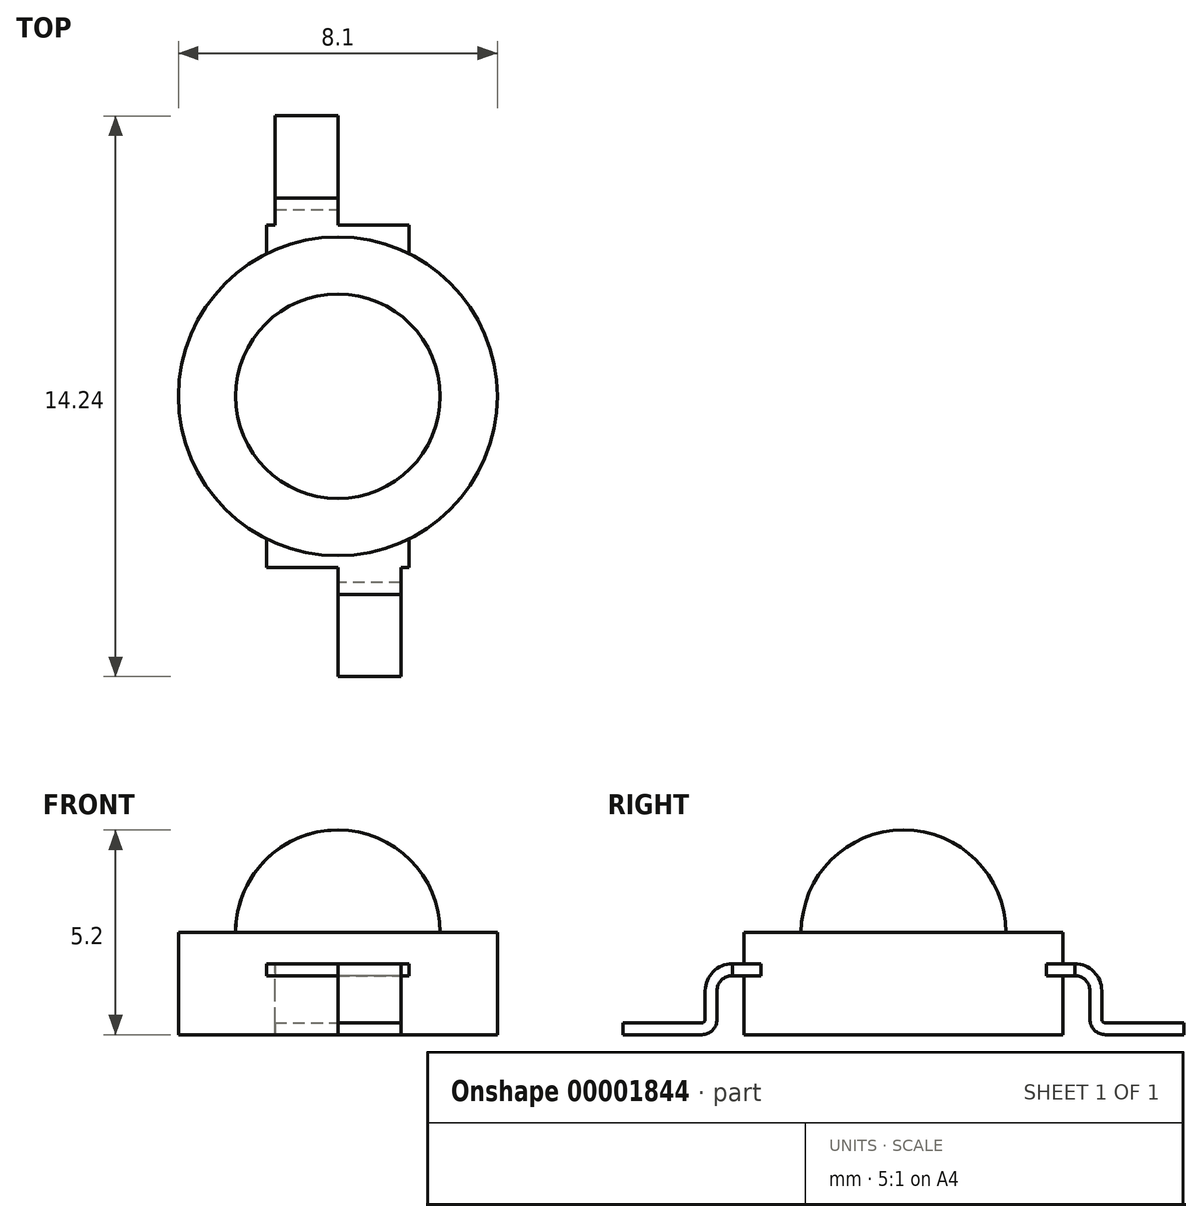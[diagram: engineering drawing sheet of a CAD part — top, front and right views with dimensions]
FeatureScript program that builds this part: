
annotation { "Feature Type Name" : "Feature", "Feature Type Description" : "" }
export const myFeature = defineFeature(function(context is Context, id is Id, definition is map)
    precondition{}
    {
        {
            var Q0;
            Q0=qCreatedBy(makeId("Front.planeOp"),FACE);
            var sketch = newSketch(context, id + "F0", { "sketchPlane" : qUnion([Q0])});
            skLineSegment(sketch, "E0", {"start": v(0, 0) * mm, "end": v(0, 5.2) * mm});
            skArc(sketch, "E1", {"start": v(0, 5.2) * mm, "mid": v(-1.84, 4.44) * mm, "end": v(-2.6, 2.6) * mm});
            skLineSegment(sketch, "E2", {"start": v(-2.6, 2.6) * mm, "end": v(-4.05, 2.6) * mm});
            skLineSegment(sketch, "E3", {"start": v(-4.05, 2.6) * mm, "end": v(-4.05, 0) * mm});
            skLineSegment(sketch, "E4", {"start": v(-4.05, 0) * mm, "end": v(0, 0) * mm});
            skSolve(sketch);
        }
        {
            var Q0;
            Q0=makeQuery(id+"F0.imprint","IMPRINT",FACE,{"disambiguationData":[TD([[makeQuery(id+"F0.imprint","IMPRINT",EDGE,{"derivedFrom":sQuery(id+"F0.wireOp",EDGE,"E0")}),1.0]])]});
            var Q1;
            Q1=sQuery(id+"F0.wireOp",EDGE,"E0");
            revolve(context, id + "F1", {"entities" : qUnion([Q0]), "axis" : qUnion([Q1]), "revolveType" : RevolveType.FULL});
        }
        {
            var Q0;
            Q0=qCreatedBy(makeId("Top.planeOp"),FACE);
            var sketch = newSketch(context, id + "F2", { "sketchPlane" : qUnion([Q0])});
            skLineSegment(sketch, "E5.bottom", {"start": v(-1.6, 7.12) * mm, "end": v(0, 7.12) * mm});
            skLineSegment(sketch, "E5.top", {"start": v(-1.6, 5.12) * mm, "end": v(0, 5.12) * mm});
            skLineSegment(sketch, "E5.left", {"start": v(-1.6, 7.12) * mm, "end": v(-1.6, 5.12) * mm});
            skLineSegment(sketch, "E5.right", {"start": v(0, 7.12) * mm, "end": v(0, 5.12) * mm});
            skLineSegment(sketch, "E6.bottom", {"start": v(-1.8, 4.05) * mm, "end": v(1.8, 4.05) * mm});
            skLineSegment(sketch, "E6.top", {"start": v(-1.8, 3.62) * mm, "end": v(1.8, 3.63) * mm});
            skLineSegment(sketch, "E6.left", {"start": v(-1.8, 4.05) * mm, "end": v(-1.8, 3.62) * mm});
            skLineSegment(sketch, "E6.right", {"start": v(1.8, 4.05) * mm, "end": v(1.8, 3.62) * mm});
            skLineSegment(sketch, "E7", {"start": v(0, 3.63) * mm, "end": v(0, 0) * mm, "construction": true});
            skLineSegment(sketch, "E8", {"start": v(0, 0) * mm, "end": v(-6.04, 0) * mm, "construction": true});
            skSolve(sketch);
        }
        {
            var Q0;
            Q0=makeQuery(id+"F2.imprint","IMPRINT",FACE,{"disambiguationData":[TD([[makeQuery(id+"F2.imprint","IMPRINT",EDGE,{"derivedFrom":sQuery(id+"F2.wireOp",EDGE,"E6.bottom")}),-1.0]])]});
            extrude(context, id + "F3", {"entities" : qUnion([Q0]), "operationType" : NewBodyOperationType.REMOVE, "endBound" : BoundingType.UP_TO_NEXT, "depth" : 25 * mm});
        }
        {
            var Q0;
            Q0=qCreatedBy(makeId("Top.planeOp"),FACE);
            cPlane(context, id + "F4", {"entities" : qUnion([Q0]), "cplaneType" : CPlaneType.OFFSET, "offset" : 1.5 * mm, "width" : 150 * mm, "height" : 150 * mm});
        }
        {
            var Q0;
            Q0=qCreatedBy(id+"F4.planeOp",FACE);
            var sketch = newSketch(context, id + "F5", { "sketchPlane" : qUnion([Q0])});
            skLineSegment(sketch, "E9.bottom", {"start": v(-1.8, 4.35) * mm, "end": v(1.8, 4.35) * mm});
            skLineSegment(sketch, "E9.top", {"start": v(-1.8, 3.63) * mm, "end": v(1.8, 3.63) * mm});
            skLineSegment(sketch, "E9.left", {"start": v(-1.8, 4.35) * mm, "end": v(-1.8, 3.62) * mm});
            skLineSegment(sketch, "E9.right", {"start": v(1.8, 4.35) * mm, "end": v(1.8, 3.62) * mm});
            skLineSegment(sketch, "E10", {"start": v(0, 3.63) * mm, "end": v(0, 0) * mm, "construction": true});
            skLineSegment(sketch, "E11", {"start": v(0, 0) * mm, "end": v(-5.3, 0) * mm, "construction": true});
            skSolve(sketch);
        }
        {
            var Q0;
            Q0 = qSketchRegion(id + "F5", true);
            extrude(context, id + "F6", {"entities" : qUnion([Q0]), "operationType" : NewBodyOperationType.ADD, "depth" : .3 * mm});
        }
        {
            var Q0;
            Q0=makeQuery(id+"F2.imprint","IMPRINT",FACE,{"disambiguationData":[TD([[makeQuery(id+"F2.imprint","IMPRINT",EDGE,{"derivedFrom":sQuery(id+"F2.wireOp",EDGE,"E5.bottom")}),-1.0]])]});
            extrude(context, id + "F7", {"entities" : qUnion([Q0]), "depth" : .3 * mm});
        }
        {
            var Q0;
            Q0=qCreatedBy(makeId("Right.planeOp"),FACE);
            var sketch = newSketch(context, id + "F8", { "sketchPlane" : qUnion([Q0])});
            skArc(sketch, "E12", {"start": v(4.74, 0.39) * mm, "mid": v(4.85, 0.11) * mm, "end": v(5.12, 0) * mm});
            skLineSegment(sketch, "E13", {"start": v(4.74, 0.39) * mm, "end": v(4.74, 1.11) * mm});
            skArc(sketch, "E14", {"start": v(4.74, 1.11) * mm, "mid": v(4.62, 1.39) * mm, "end": v(4.35, 1.5) * mm});
            skSolve(sketch);
        }
        {
            var Q0;
            Q0=makeQuery(id+"F7.opExtrude","SWEPT_FACE",FACE,{"disambiguationData":[OSD([sQuery(id+"F2.wireOp",EDGE,"E5.top")])]});
            var Q1;
            Q1=sQuery(id+"F8.wireOp",EDGE,"E12");
            var Q2;
            Q2=sQuery(id+"F8.wireOp",EDGE,"E13");
            var Q3;
            Q3=sQuery(id+"F8.wireOp",EDGE,"E14");
            sweep(context, id + "F9", {"operationType" : NewBodyOperationType.ADD, "profiles" : qUnion([Q0]), "path" : qUnion([Q1, Q2, Q3])});
        }
        {
            var Q0;
            Q0=makeQuery(id+"F1.opRevolve","SWEPT_BODY",BODY,{"disambiguationData":[OSD([sQuery(id+"F0.wireOp",EDGE,"E0"),sQuery(id+"F0.wireOp",EDGE,"E1"),sQuery(id+"F0.wireOp",EDGE,"E2"),sQuery(id+"F0.wireOp",EDGE,"E3"),sQuery(id+"F0.wireOp",EDGE,"E4")])]});
            var Q1;
            {var subQ1=sQuery(id+"F5.wireOp",EDGE,"E9.left");Q1=makeQuery(id+"F9fP5FhXNjzQOyg_1.1.F3.boolean.opBoolean","SPLIT",FACE,{"disambiguationData":[TD([makeQuery(id+"F6.opExtrude","SWEPT_FACE",FACE,{"disambiguationData":[OSD([subQ1])]})])],"derivedFrom":makeQuery(id+"F1.opRevolve","SWEPT_FACE",FACE,{"disambiguationData":[OSD([sQuery(id+"F0.wireOp",EDGE,"E3")])]})});}
            var Q2;
            Q2=makeQuery(id+"F1.opRevolve","SWEPT_BODY",BODY,{"disambiguationData":[OSD([sQuery(id+"F0.wireOp",EDGE,"E0"),sQuery(id+"F0.wireOp",EDGE,"E1"),sQuery(id+"F0.wireOp",EDGE,"E2"),sQuery(id+"F0.wireOp",EDGE,"E3"),sQuery(id+"F0.wireOp",EDGE,"E4")])]});
            circularPattern(context, id + "F10", {"operationType" : NewBodyOperationType.ADD, "entities" : qUnion([Q0]), "axis" : qUnion([Q1]), "angle" : 360 * degree, "instanceCount" : 2, "equalSpace" : true});
        }
    });
